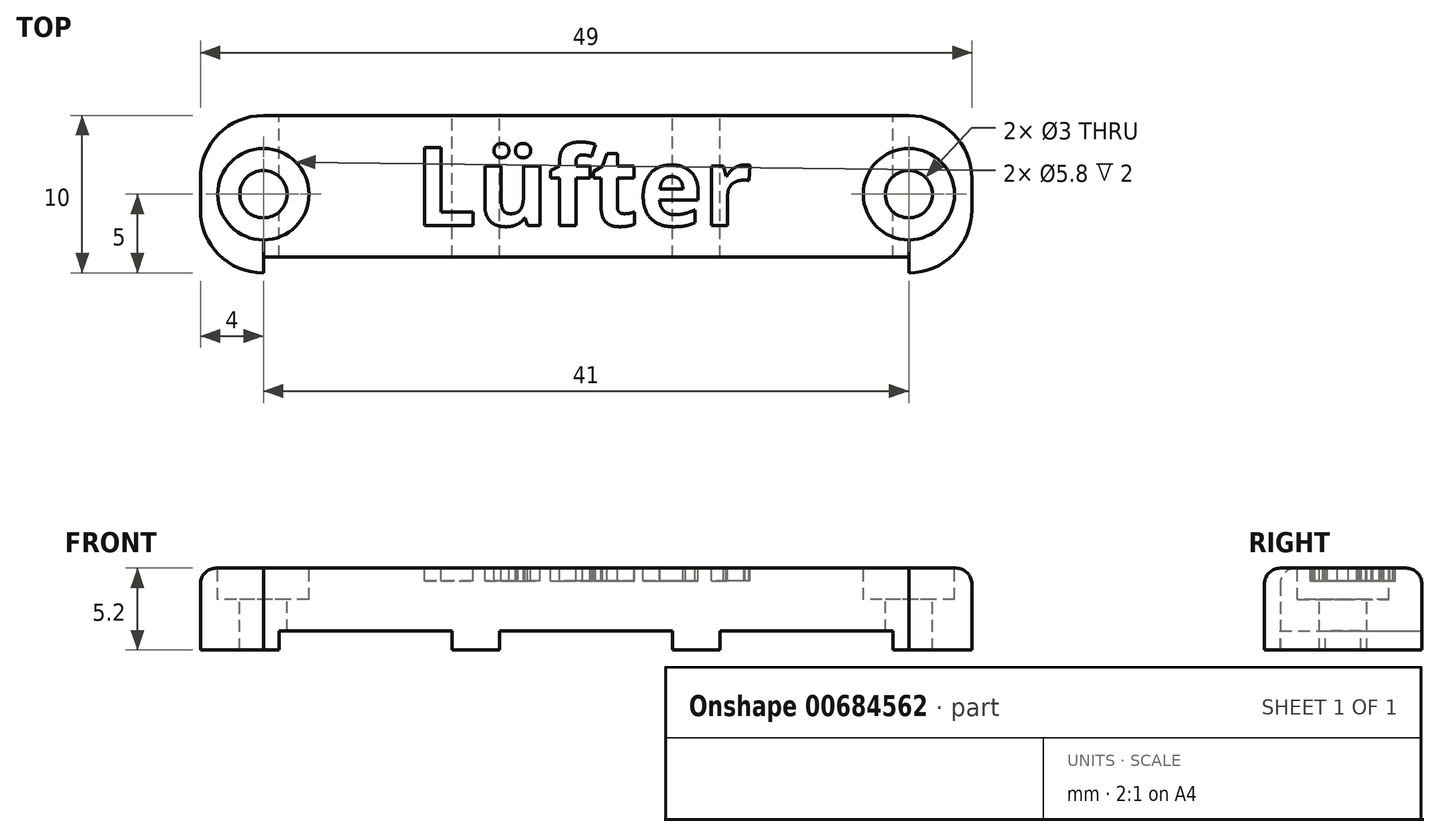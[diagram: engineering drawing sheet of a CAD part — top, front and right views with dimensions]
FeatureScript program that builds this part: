
annotation { "Feature Type Name" : "Feature", "Feature Type Description" : "" }
export const myFeature = defineFeature(function(context is Context, id is Id, definition is map)
    precondition{}
    {
        {
            var Q0;
            Q0=qCreatedBy(makeId("Top.planeOp"),FACE);
            var sketch = newSketch(context, id + "F0", { "sketchPlane" : qUnion([Q0])});
            skLineSegment(sketch, "E0", {"start": v(0, 0) * mm, "end": v(0, 10) * mm});
            skLineSegment(sketch, "E1", {"start": v(0, 10) * mm, "end": v(49, 10) * mm});
            skLineSegment(sketch, "E2", {"start": v(49, 10) * mm, "end": v(49, 0) * mm});
            skLineSegment(sketch, "E3", {"start": v(49, 0) * mm, "end": v(45, 0) * mm});
            skLineSegment(sketch, "E4", {"start": v(45, 0) * mm, "end": v(45, 1) * mm});
            skLineSegment(sketch, "E5", {"start": v(45, 1) * mm, "end": v(4, 1) * mm});
            skLineSegment(sketch, "E6", {"start": v(4, 1) * mm, "end": v(4, 0) * mm});
            skLineSegment(sketch, "E7", {"start": v(4, 0) * mm, "end": v(0, 0) * mm});
            skSolve(sketch);
        }
        {
            var Q0;
            Q0=makeQuery(id+"F0.imprint","IMPRINT",FACE,{"disambiguationData":[TD([[makeQuery(id+"F0.imprint","IMPRINT",EDGE,{"derivedFrom":sQuery(id+"F0.wireOp",EDGE,"E0")}),-1.0]])]});
            extrude(context, id + "F1", {"entities" : qUnion([Q0]), "depth" : 4 * mm});
        }
        {
            var Q0;
            Q0=makeQuery(id+"F1.opExtrude","CAP_FACE",FACE,{"disambiguationData":[OSD([sQuery(id+"F0.wireOp",EDGE,"E0"),sQuery(id+"F0.wireOp",EDGE,"E1"),sQuery(id+"F0.wireOp",EDGE,"E2"),sQuery(id+"F0.wireOp",EDGE,"E3"),sQuery(id+"F0.wireOp",EDGE,"E4"),sQuery(id+"F0.wireOp",EDGE,"E5"),sQuery(id+"F0.wireOp",EDGE,"E6"),sQuery(id+"F0.wireOp",EDGE,"E7")])],"isStart":true});
            var sketch = newSketch(context, id + "F2", { "sketchPlane" : qUnion([Q0])});
            skLineSegment(sketch, "E8.bottom", {"start": v(0, 0) * mm, "end": v(5, 0) * mm});
            skLineSegment(sketch, "E8.top", {"start": v(0, -10) * mm, "end": v(5, -10) * mm});
            skLineSegment(sketch, "E8.left", {"start": v(0, 0) * mm, "end": v(0, -10) * mm});
            skLineSegment(sketch, "E8.right", {"start": v(5, 0) * mm, "end": v(5, -10) * mm});
            skLineSegment(sketch, "E9.bottom", {"start": v(49, 0) * mm, "end": v(44, 0) * mm});
            skLineSegment(sketch, "E9.top", {"start": v(49, -10) * mm, "end": v(44, -10) * mm});
            skLineSegment(sketch, "E9.left", {"start": v(49, 0) * mm, "end": v(49, -10) * mm});
            skLineSegment(sketch, "E9.right", {"start": v(44, 0) * mm, "end": v(44, -10) * mm});
            skLineSegment(sketch, "E10.bottom", {"start": v(16, -1) * mm, "end": v(19, -1) * mm});
            skLineSegment(sketch, "E10.top", {"start": v(16, -10) * mm, "end": v(19, -10) * mm});
            skLineSegment(sketch, "E10.left", {"start": v(16, -1) * mm, "end": v(16, -10) * mm});
            skLineSegment(sketch, "E10.right", {"start": v(19, -1) * mm, "end": v(19, -10) * mm});
            skLineSegment(sketch, "E11.bottom", {"start": v(30, -1) * mm, "end": v(33, -1) * mm});
            skLineSegment(sketch, "E11.top", {"start": v(30, -10) * mm, "end": v(33, -10) * mm});
            skLineSegment(sketch, "E11.left", {"start": v(30, -1) * mm, "end": v(30, -10) * mm});
            skLineSegment(sketch, "E11.right", {"start": v(33, -1) * mm, "end": v(33, -10) * mm});
            skSolve(sketch);
        }
        {
            var Q0;
            {var subQ1=sQuery(id+"F2.wireOp",EDGE,"E8.top");Q0=makeQuery(id+"F2.imprint","IMPRINT",FACE,{"disambiguationData":[TD([[makeQuery(id+"F2.imprint","IMPRINT",EDGE,{"derivedFrom":subQ1}),1.0]])]});}
            var Q1;
            Q1=makeQuery(id+"F2.imprint","IMPRINT",FACE,{"disambiguationData":[TD([[makeQuery(id+"F2.imprint","IMPRINT",EDGE,{"derivedFrom":sQuery(id+"F2.wireOp",EDGE,"E10.bottom")}),1.0]])]});
            var Q2;
            Q2=makeQuery(id+"F2.imprint","IMPRINT",FACE,{"disambiguationData":[TD([[makeQuery(id+"F2.imprint","IMPRINT",EDGE,{"derivedFrom":sQuery(id+"F2.wireOp",EDGE,"E11.bottom")}),1.0]])]});
            var Q3;
            {var subQ2=sQuery(id+"F2.wireOp",EDGE,"E9.top");Q3=makeQuery(id+"F2.imprint","IMPRINT",FACE,{"disambiguationData":[TD([[makeQuery(id+"F2.imprint","IMPRINT",EDGE,{"derivedFrom":subQ2}),1.0]])]});}
            extrude(context, id + "F3", {"entities" : qUnion([Q0, Q1, Q2, Q3]), "operationType" : NewBodyOperationType.ADD, "depth" : 1.2 * mm});
        }
        {
            var Q0;
            Q0=makeQuery(id+"F1.opExtrude","CAP_FACE",FACE,{"disambiguationData":[OSD([sQuery(id+"F0.wireOp",EDGE,"E0"),sQuery(id+"F0.wireOp",EDGE,"E1"),sQuery(id+"F0.wireOp",EDGE,"E2"),sQuery(id+"F0.wireOp",EDGE,"E3"),sQuery(id+"F0.wireOp",EDGE,"E4"),sQuery(id+"F0.wireOp",EDGE,"E5"),sQuery(id+"F0.wireOp",EDGE,"E6"),sQuery(id+"F0.wireOp",EDGE,"E7")])],"isStart":false});
            var sketch = newSketch(context, id + "F4", { "sketchPlane" : qUnion([Q0])});
            skCircle(sketch, "E12", {"center": v(4, 5) * mm, "radius": 1.5 * mm});
            skCircle(sketch, "E13", {"center": v(45, 5) * mm, "radius": 1.5 * mm});
            skSolve(sketch);
        }
        {
            var Q0;
            Q0=makeQuery(id+"F4.imprint","IMPRINT",FACE,{"disambiguationData":[TD([[makeQuery(id+"F4.imprint","IMPRINT",EDGE,{"derivedFrom":sQuery(id+"F4.wireOp",EDGE,"E12")}),1.0]])]});
            var Q1;
            Q1=makeQuery(id+"F4.imprint","IMPRINT",FACE,{"disambiguationData":[TD([[makeQuery(id+"F4.imprint","IMPRINT",EDGE,{"derivedFrom":sQuery(id+"F4.wireOp",EDGE,"E13")}),1.0]])]});
            extrude(context, id + "F5", {"entities" : qUnion([Q0, Q1]), "operationType" : NewBodyOperationType.REMOVE, "endBound" : BoundingType.THROUGH_ALL, "oppositeDirection" : true, "depth" : 25 * mm});
        }
        {
            var Q0;
            Q0=makeQuery(id+"F3.boolean.opBoolean","MERGE",EDGE,{"derivedFrom":[makeQuery(id+"F1.opExtrude","SWEPT_EDGE",EDGE,{"disambiguationData":[OSD([sQuery(id+"F0.wireOp",EDGE,"E2"),sQuery(id+"F0.wireOp",EDGE,"E3")])]}),makeQuery(id+"F3.opExtrude","SWEPT_EDGE",EDGE,{"disambiguationData":[OSD([sQuery(id+"F2.wireOp",EDGE,"E9.bottom"),sQuery(id+"F2.wireOp",EDGE,"E9.left")])]})]});
            var Q1;
            Q1=makeQuery(id+"F3.boolean.opBoolean","MERGE",EDGE,{"derivedFrom":[makeQuery(id+"F1.opExtrude","SWEPT_EDGE",EDGE,{"disambiguationData":[OSD([sQuery(id+"F0.wireOp",EDGE,"E1"),sQuery(id+"F0.wireOp",EDGE,"E2")])]}),makeQuery(id+"F3.opExtrude","SWEPT_EDGE",EDGE,{"disambiguationData":[OSD([sQuery(id+"F2.wireOp",EDGE,"E9.top"),sQuery(id+"F2.wireOp",EDGE,"E9.left")])]})]});
            var Q2;
            Q2=makeQuery(id+"F3.boolean.opBoolean","MERGE",EDGE,{"derivedFrom":[makeQuery(id+"F1.opExtrude","SWEPT_EDGE",EDGE,{"disambiguationData":[OSD([sQuery(id+"F0.wireOp",EDGE,"E0"),sQuery(id+"F0.wireOp",EDGE,"E7")])]}),makeQuery(id+"F3.opExtrude","SWEPT_EDGE",EDGE,{"disambiguationData":[OSD([sQuery(id+"F2.wireOp",EDGE,"E8.bottom"),sQuery(id+"F2.wireOp",EDGE,"E8.left")])]})]});
            var Q3;
            Q3=makeQuery(id+"F3.boolean.opBoolean","MERGE",EDGE,{"derivedFrom":[makeQuery(id+"F1.opExtrude","SWEPT_EDGE",EDGE,{"disambiguationData":[OSD([sQuery(id+"F0.wireOp",EDGE,"E0"),sQuery(id+"F0.wireOp",EDGE,"E1")])]}),makeQuery(id+"F3.opExtrude","SWEPT_EDGE",EDGE,{"disambiguationData":[OSD([sQuery(id+"F2.wireOp",EDGE,"E8.top"),sQuery(id+"F2.wireOp",EDGE,"E8.left")])]})]});
            fillet(context, id + "F6", {"entities" : qUnion([Q0, Q1, Q2, Q3]), "radius" : 4 * mm, "tangentPropagation" : true, "allowEdgeOverflow" : false});
        }
        {
            var Q0;
            Q0=makeQuery(id+"F1.opExtrude","CAP_EDGE",EDGE,{"disambiguationData":[OSD([sQuery(id+"F0.wireOp",EDGE,"E5")])],"isStart":false});
            var Q1;
            Q1=makeQuery(id+"F1.opExtrude","CAP_EDGE",EDGE,{"disambiguationData":[OSD([sQuery(id+"F0.wireOp",EDGE,"E1")])],"isStart":false});
            var Q2;
            {var subQ0=sQuery(id+"F0.wireOp",EDGE,"E7");var subQ1=sQuery(id+"F0.wireOp",EDGE,"E0");Q2=makeQuery(id+"F6.opFillet","BLEND_EDGE",EDGE,{"blendedFrom":[makeQuery(id+"F3.boolean.opBoolean","MERGE",EDGE,{"derivedFrom":[makeQuery(id+"F1.opExtrude","SWEPT_EDGE",EDGE,{"disambiguationData":[OSD([subQ1,subQ0])]}),makeQuery(id+"F3.opExtrude","SWEPT_EDGE",EDGE,{"disambiguationData":[OSD([sQuery(id+"F2.wireOp",EDGE,"E8.bottom"),sQuery(id+"F2.wireOp",EDGE,"E8.left")])]})]}),makeQuery(id+"F1.opExtrude","CAP_FACE",FACE,{"disambiguationData":[OSD([subQ1,sQuery(id+"F0.wireOp",EDGE,"E1"),sQuery(id+"F0.wireOp",EDGE,"E2"),sQuery(id+"F0.wireOp",EDGE,"E3"),sQuery(id+"F0.wireOp",EDGE,"E4"),sQuery(id+"F0.wireOp",EDGE,"E5"),sQuery(id+"F0.wireOp",EDGE,"E6"),subQ0])],"isStart":false})],"blendedInto":[makeQuery(id+"F1.opExtrude","CAP_FACE",FACE,{"disambiguationData":[OSD([subQ1,sQuery(id+"F0.wireOp",EDGE,"E1"),sQuery(id+"F0.wireOp",EDGE,"E2"),sQuery(id+"F0.wireOp",EDGE,"E3"),sQuery(id+"F0.wireOp",EDGE,"E4"),sQuery(id+"F0.wireOp",EDGE,"E5"),sQuery(id+"F0.wireOp",EDGE,"E6"),subQ0])],"isStart":false})]});}
            var Q3;
            Q3=makeQuery(id+"F1.opExtrude","CAP_EDGE",EDGE,{"disambiguationData":[OSD([sQuery(id+"F0.wireOp",EDGE,"E0")])],"isStart":false});
            var Q4;
            {var subQ0=sQuery(id+"F0.wireOp",EDGE,"E1");var subQ1=sQuery(id+"F0.wireOp",EDGE,"E0");Q4=makeQuery(id+"F6.opFillet","BLEND_EDGE",EDGE,{"blendedFrom":[makeQuery(id+"F3.boolean.opBoolean","MERGE",EDGE,{"derivedFrom":[makeQuery(id+"F1.opExtrude","SWEPT_EDGE",EDGE,{"disambiguationData":[OSD([subQ1,subQ0])]}),makeQuery(id+"F3.opExtrude","SWEPT_EDGE",EDGE,{"disambiguationData":[OSD([sQuery(id+"F2.wireOp",EDGE,"E8.top"),sQuery(id+"F2.wireOp",EDGE,"E8.left")])]})]}),makeQuery(id+"F1.opExtrude","CAP_FACE",FACE,{"disambiguationData":[OSD([subQ1,subQ0,sQuery(id+"F0.wireOp",EDGE,"E2"),sQuery(id+"F0.wireOp",EDGE,"E3"),sQuery(id+"F0.wireOp",EDGE,"E4"),sQuery(id+"F0.wireOp",EDGE,"E5"),sQuery(id+"F0.wireOp",EDGE,"E6"),sQuery(id+"F0.wireOp",EDGE,"E7")])],"isStart":false})],"blendedInto":[makeQuery(id+"F1.opExtrude","CAP_FACE",FACE,{"disambiguationData":[OSD([subQ1,subQ0,sQuery(id+"F0.wireOp",EDGE,"E2"),sQuery(id+"F0.wireOp",EDGE,"E3"),sQuery(id+"F0.wireOp",EDGE,"E4"),sQuery(id+"F0.wireOp",EDGE,"E5"),sQuery(id+"F0.wireOp",EDGE,"E6"),sQuery(id+"F0.wireOp",EDGE,"E7")])],"isStart":false})]});}
            var Q5;
            {var subQ0=sQuery(id+"F0.wireOp",EDGE,"E3");var subQ1=sQuery(id+"F0.wireOp",EDGE,"E2");Q5=makeQuery(id+"F6.opFillet","BLEND_EDGE",EDGE,{"blendedFrom":[makeQuery(id+"F3.boolean.opBoolean","MERGE",EDGE,{"derivedFrom":[makeQuery(id+"F1.opExtrude","SWEPT_EDGE",EDGE,{"disambiguationData":[OSD([subQ1,subQ0])]}),makeQuery(id+"F3.opExtrude","SWEPT_EDGE",EDGE,{"disambiguationData":[OSD([sQuery(id+"F2.wireOp",EDGE,"E9.bottom"),sQuery(id+"F2.wireOp",EDGE,"E9.left")])]})]}),makeQuery(id+"F1.opExtrude","CAP_FACE",FACE,{"disambiguationData":[OSD([sQuery(id+"F0.wireOp",EDGE,"E0"),sQuery(id+"F0.wireOp",EDGE,"E1"),subQ1,subQ0,sQuery(id+"F0.wireOp",EDGE,"E4"),sQuery(id+"F0.wireOp",EDGE,"E5"),sQuery(id+"F0.wireOp",EDGE,"E6"),sQuery(id+"F0.wireOp",EDGE,"E7")])],"isStart":false})],"blendedInto":[makeQuery(id+"F1.opExtrude","CAP_FACE",FACE,{"disambiguationData":[OSD([sQuery(id+"F0.wireOp",EDGE,"E0"),sQuery(id+"F0.wireOp",EDGE,"E1"),subQ1,subQ0,sQuery(id+"F0.wireOp",EDGE,"E4"),sQuery(id+"F0.wireOp",EDGE,"E5"),sQuery(id+"F0.wireOp",EDGE,"E6"),sQuery(id+"F0.wireOp",EDGE,"E7")])],"isStart":false})]});}
            var Q6;
            Q6=makeQuery(id+"F1.opExtrude","CAP_EDGE",EDGE,{"disambiguationData":[OSD([sQuery(id+"F0.wireOp",EDGE,"E2")])],"isStart":false});
            var Q7;
            {var subQ0=sQuery(id+"F0.wireOp",EDGE,"E2");var subQ1=sQuery(id+"F0.wireOp",EDGE,"E1");Q7=makeQuery(id+"F6.opFillet","BLEND_EDGE",EDGE,{"blendedFrom":[makeQuery(id+"F3.boolean.opBoolean","MERGE",EDGE,{"derivedFrom":[makeQuery(id+"F1.opExtrude","SWEPT_EDGE",EDGE,{"disambiguationData":[OSD([subQ1,subQ0])]}),makeQuery(id+"F3.opExtrude","SWEPT_EDGE",EDGE,{"disambiguationData":[OSD([sQuery(id+"F2.wireOp",EDGE,"E9.top"),sQuery(id+"F2.wireOp",EDGE,"E9.left")])]})]}),makeQuery(id+"F1.opExtrude","CAP_FACE",FACE,{"disambiguationData":[OSD([sQuery(id+"F0.wireOp",EDGE,"E0"),subQ1,subQ0,sQuery(id+"F0.wireOp",EDGE,"E3"),sQuery(id+"F0.wireOp",EDGE,"E4"),sQuery(id+"F0.wireOp",EDGE,"E5"),sQuery(id+"F0.wireOp",EDGE,"E6"),sQuery(id+"F0.wireOp",EDGE,"E7")])],"isStart":false})],"blendedInto":[makeQuery(id+"F1.opExtrude","CAP_FACE",FACE,{"disambiguationData":[OSD([sQuery(id+"F0.wireOp",EDGE,"E0"),subQ1,subQ0,sQuery(id+"F0.wireOp",EDGE,"E3"),sQuery(id+"F0.wireOp",EDGE,"E4"),sQuery(id+"F0.wireOp",EDGE,"E5"),sQuery(id+"F0.wireOp",EDGE,"E6"),sQuery(id+"F0.wireOp",EDGE,"E7")])],"isStart":false})]});}
            fillet(context, id + "F7", {"entities" : qUnion([Q0, Q1, Q2, Q3, Q4, Q5, Q6, Q7]), "radius" : 1 * mm, "tangentPropagation" : true, "allowEdgeOverflow" : false});
        }
        {
            var Q0;
            Q0=makeQuery(id+"F1.opExtrude","CAP_FACE",FACE,{"disambiguationData":[OSD([sQuery(id+"F0.wireOp",EDGE,"E0"),sQuery(id+"F0.wireOp",EDGE,"E1"),sQuery(id+"F0.wireOp",EDGE,"E2"),sQuery(id+"F0.wireOp",EDGE,"E3"),sQuery(id+"F0.wireOp",EDGE,"E4"),sQuery(id+"F0.wireOp",EDGE,"E5"),sQuery(id+"F0.wireOp",EDGE,"E6"),sQuery(id+"F0.wireOp",EDGE,"E7")])],"isStart":false});
            var sketch = newSketch(context, id + "F8", { "sketchPlane" : qUnion([Q0])});
            skText(sketch, "E14", { "text": "Lüfter", "fontName": "OpenSans-Bold.ttf"});
            const initialGuessF8  = {"E14": [0.01362, 0.003, 1, 0, 0.005]};
            skSetInitialGuess(sketch, initialGuessF8);
            skSolve(sketch);
        }
        {
            var Q0;
            Q0=makeQuery(id+"F8.imprint","IMPRINT",FACE,{"disambiguationData":[TD([[makeQuery(id+"F8.imprint","IMPRINT",EDGE,{"derivedFrom":sQuery(id+"F8.wireOp",EDGE,"E14.sketch_text.stroke-0")}),-1.0]])]});
            var Q1;
            Q1=makeQuery(id+"F8.imprint","IMPRINT",FACE,{"disambiguationData":[TD([[makeQuery(id+"F8.imprint","IMPRINT",EDGE,{"derivedFrom":sQuery(id+"F8.wireOp",EDGE,"E14.sketch_text.stroke-6")}),-1.0]])]});
            var Q2;
            Q2=makeQuery(id+"F8.imprint","IMPRINT",FACE,{"disambiguationData":[TD([[makeQuery(id+"F8.imprint","IMPRINT",EDGE,{"derivedFrom":sQuery(id+"F8.wireOp",EDGE,"E14.sketch_text.stroke-23")}),-1.0]])]});
            var Q3;
            Q3=makeQuery(id+"F8.imprint","IMPRINT",FACE,{"disambiguationData":[TD([[makeQuery(id+"F8.imprint","IMPRINT",EDGE,{"derivedFrom":sQuery(id+"F8.wireOp",EDGE,"E14.sketch_text.stroke-31")}),-1.0]])]});
            var Q4;
            Q4=makeQuery(id+"F8.imprint","IMPRINT",FACE,{"disambiguationData":[TD([[makeQuery(id+"F8.imprint","IMPRINT",EDGE,{"derivedFrom":sQuery(id+"F8.wireOp",EDGE,"E14.sketch_text.stroke-39")}),-1.0]])]});
            var Q5;
            Q5=makeQuery(id+"F8.imprint","IMPRINT",FACE,{"disambiguationData":[TD([[makeQuery(id+"F8.imprint","IMPRINT",EDGE,{"derivedFrom":sQuery(id+"F8.wireOp",EDGE,"E14.sketch_text.stroke-57")}),-1.0]])]});
            var Q6;
            Q6=makeQuery(id+"F8.imprint","IMPRINT",FACE,{"disambiguationData":[TD([[makeQuery(id+"F8.imprint","IMPRINT",EDGE,{"derivedFrom":sQuery(id+"F8.wireOp",EDGE,"E14.sketch_text.stroke-75")}),-1.0]])]});
            var Q7;
            Q7=makeQuery(id+"F8.imprint","IMPRINT",FACE,{"disambiguationData":[TD([[makeQuery(id+"F8.imprint","IMPRINT",EDGE,{"derivedFrom":sQuery(id+"F8.wireOp",EDGE,"E14.sketch_text.stroke-95")}),-1.0]])]});
            extrude(context, id + "F9", {"entities" : qUnion([Q0, Q1, Q2, Q3, Q4, Q5, Q6, Q7]), "operationType" : NewBodyOperationType.REMOVE, "oppositeDirection" : true, "depth" : 0.8 * mm});
        }
        {
            var Q0;
            {var subQ1=sQuery(id+"F0.wireOp",EDGE,"E7");var subQ2=sQuery(id+"F0.wireOp",EDGE,"E6");var subQ3=sQuery(id+"F0.wireOp",EDGE,"E5");var subQ4=sQuery(id+"F0.wireOp",EDGE,"E4");var subQ5=sQuery(id+"F0.wireOp",EDGE,"E3");var subQ6=sQuery(id+"F0.wireOp",EDGE,"E2");var subQ7=sQuery(id+"F0.wireOp",EDGE,"E1");var subQ8=sQuery(id+"F0.wireOp",EDGE,"E0");Q0=makeQuery(id+"F9.boolean.opBoolean","SPLIT",FACE,{"disambiguationData":[TD([makeQuery(id+"F1.opExtrude","SWEPT_FACE",FACE,{"disambiguationData":[OSD([subQ4])]})])],"derivedFrom":makeQuery(id+"F1.opExtrude","CAP_FACE",FACE,{"disambiguationData":[OSD([subQ8,subQ7,subQ6,subQ5,subQ4,subQ3,subQ2,subQ1])],"isStart":false})});}
            var sketch = newSketch(context, id + "F10", { "sketchPlane" : qUnion([Q0])});
            skCircle(sketch, "E15", {"center": v(4, 5) * mm, "radius": 2.9 * mm});
            skCircle(sketch, "E16", {"center": v(45, 5) * mm, "radius": 2.9 * mm});
            skSolve(sketch);
        }
        {
            var Q0;
            Q0=makeQuery(id+"F10.imprint","IMPRINT",FACE,{"disambiguationData":[TD([[makeQuery(id+"F10.imprint","IMPRINT",EDGE,{"derivedFrom":sQuery(id+"F10.wireOp",EDGE,"E15")}),1.0]])]});
            var Q1;
            Q1=makeQuery(id+"F10.imprint","IMPRINT",FACE,{"disambiguationData":[TD([[makeQuery(id+"F10.imprint","IMPRINT",EDGE,{"derivedFrom":sQuery(id+"F10.wireOp",EDGE,"E16")}),1.0]])]});
            extrude(context, id + "F11", {"entities" : qUnion([Q0, Q1]), "operationType" : NewBodyOperationType.REMOVE, "oppositeDirection" : true, "depth" : 2 * mm});
        }
    });
